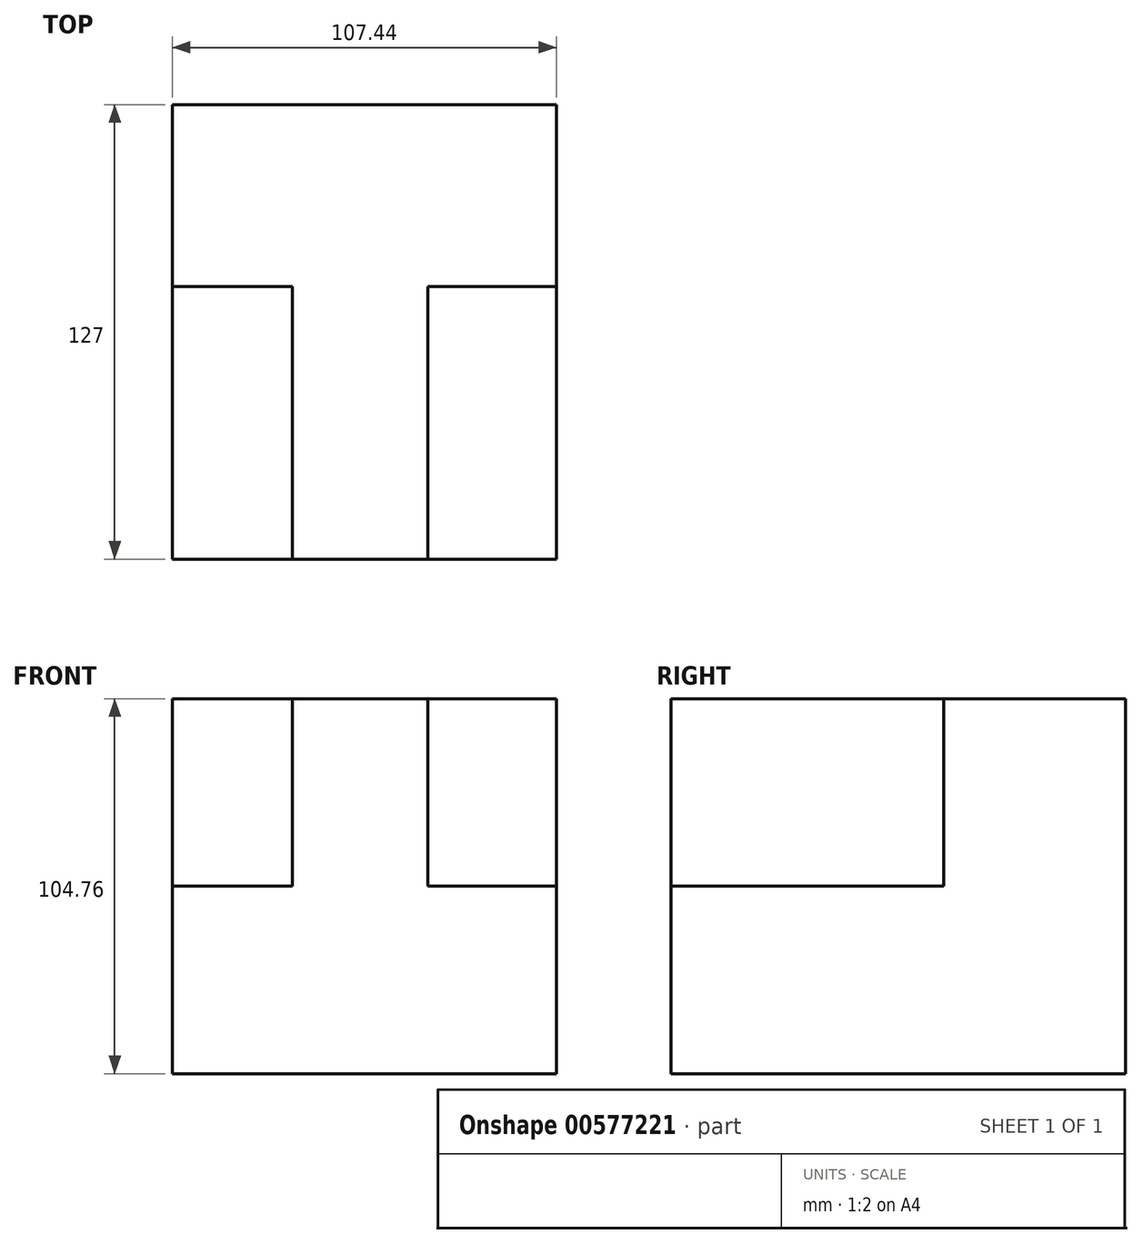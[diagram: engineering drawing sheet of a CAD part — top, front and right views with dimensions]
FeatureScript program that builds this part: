
annotation { "Feature Type Name" : "Feature", "Feature Type Description" : "" }
export const myFeature = defineFeature(function(context is Context, id is Id, definition is map)
    precondition{}
    {
        {
            var Q0;
            Q0=qCreatedBy(makeId("Front.planeOp"),FACE);
            var sketch = newSketch(context, id + "F0", { "sketchPlane" : qUnion([Q0])});
            skLineSegment(sketch, "E0.bottom", {"start": v(-54.43, 51.9) * mm, "end": v(53, 51.9) * mm});
            skLineSegment(sketch, "E0.top", {"start": v(-54.43, -52.86) * mm, "end": v(53, -52.86) * mm});
            skLineSegment(sketch, "E0.left", {"start": v(-54.43, 51.9) * mm, "end": v(-54.43, -52.86) * mm});
            skLineSegment(sketch, "E0.right", {"start": v(53, 51.9) * mm, "end": v(53, -52.86) * mm});
            skSolve(sketch);
        }
        {
            var Q0;
            Q0=makeQuery(id+"F0.imprint","IMPRINT",FACE,{"disambiguationData":[TD([[makeQuery(id+"F0.imprint","IMPRINT",EDGE,{"derivedFrom":sQuery(id+"F0.wireOp",EDGE,"E0.bottom")}),-1.0]])]});
            extrude(context, id + "F1", {"entities" : qUnion([Q0]), "depth" : -50.8 * mm, "offsetDistance" : 25.4 * mm});
        }
        {
            var Q0;
            Q0=makeQuery(id+"F1.opExtrude","CAP_FACE",FACE,{"disambiguationData":[OSD([sQuery(id+"F0.wireOp",EDGE,"E0.bottom"),sQuery(id+"F0.wireOp",EDGE,"E0.top"),sQuery(id+"F0.wireOp",EDGE,"E0.left"),sQuery(id+"F0.wireOp",EDGE,"E0.right")])],"isStart":true});
            var sketch = newSketch(context, id + "F2", { "sketchPlane" : qUnion([Q0])});
            skLineSegment(sketch, "E1.bottom", {"start": v(-20.78, 51.9) * mm, "end": v(17, 51.9) * mm});
            skLineSegment(sketch, "E1.top", {"start": v(-20.78, -52.86) * mm, "end": v(17, -52.86) * mm});
            skLineSegment(sketch, "E1.left", {"start": v(-20.78, 51.9) * mm, "end": v(-20.78, -52.86) * mm});
            skLineSegment(sketch, "E1.right", {"start": v(17, 51.9) * mm, "end": v(17, -52.86) * mm});
            skLineSegment(sketch, "E2.bottom", {"start": v(17, -0.48) * mm, "end": v(53, -0.48) * mm});
            skLineSegment(sketch, "E2.top", {"start": v(17, -52.86) * mm, "end": v(53, -52.86) * mm});
            skLineSegment(sketch, "E2.left", {"start": v(17, -0.48) * mm, "end": v(17, -52.86) * mm});
            skLineSegment(sketch, "E2.right", {"start": v(53, -0.48) * mm, "end": v(53, -52.86) * mm});
            skLineSegment(sketch, "E3.bottom", {"start": v(-20.78, -0.48) * mm, "end": v(-54.43, -0.48) * mm});
            skLineSegment(sketch, "E3.top", {"start": v(-20.78, -52.86) * mm, "end": v(-54.43, -52.86) * mm});
            skLineSegment(sketch, "E3.left", {"start": v(-20.78, -0.48) * mm, "end": v(-20.78, -52.86) * mm});
            skLineSegment(sketch, "E3.right", {"start": v(-54.43, -0.48) * mm, "end": v(-54.43, -52.86) * mm});
            skSolve(sketch);
        }
        {
            var Q0;
            Q0=makeQuery(id+"F2.imprint","IMPRINT",FACE,{"disambiguationData":[TD([[makeQuery(id+"F2.imprint","IMPRINT",EDGE,{"derivedFrom":sQuery(id+"F2.wireOp",EDGE,"E1.bottom")}),-1.0]])]});
            var Q1;
            Q1=makeQuery(id+"F2.imprint","IMPRINT",FACE,{"disambiguationData":[TD([[makeQuery(id+"F2.imprint","IMPRINT",EDGE,{"derivedFrom":sQuery(id+"F2.wireOp",EDGE,"E2.bottom")}),-1.0]])]});
            var Q2;
            Q2=makeQuery(id+"F2.imprint","IMPRINT",FACE,{"disambiguationData":[TD([[makeQuery(id+"F2.imprint","IMPRINT",EDGE,{"derivedFrom":sQuery(id+"F2.wireOp",EDGE,"E3.bottom")}),1.0]])]});
            extrude(context, id + "F3", {"entities" : qUnion([Q0, Q1, Q2]), "operationType" : NewBodyOperationType.ADD, "depth" : 76.2 * mm, "offsetDistance" : 25.4 * mm});
        }
    });
